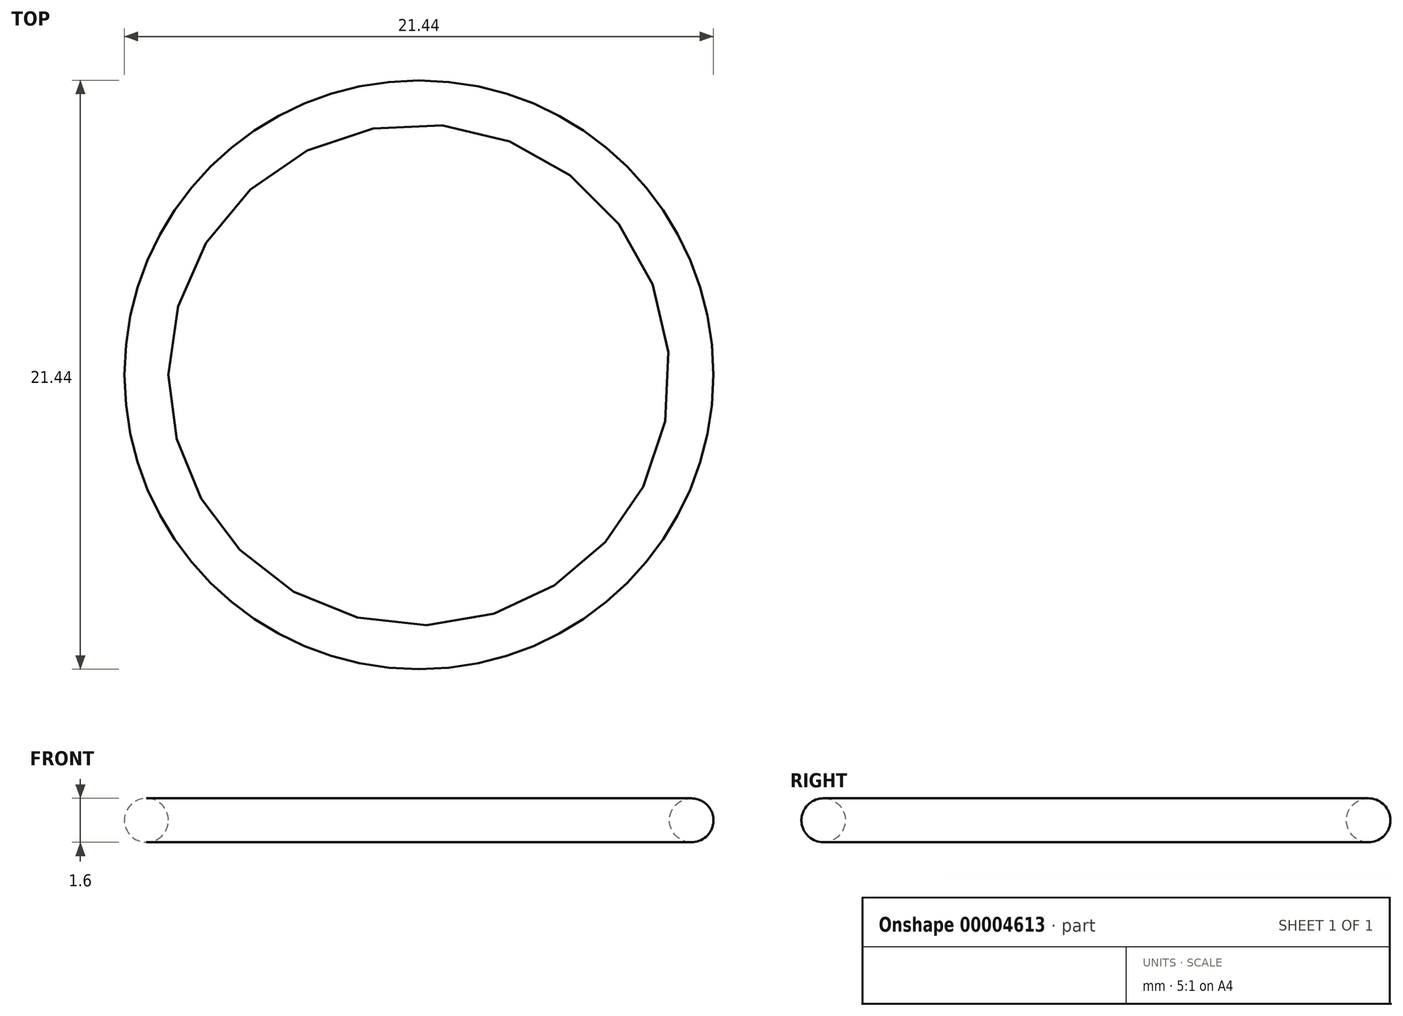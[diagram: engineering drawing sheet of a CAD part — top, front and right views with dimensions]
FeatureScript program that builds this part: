
annotation { "Feature Type Name" : "Feature", "Feature Type Description" : "" }
export const myFeature = defineFeature(function(context is Context, id is Id, definition is map)
    precondition{}
    {
        {
            var Q0;
            Q0=qCreatedBy(makeId("Front.planeOp"),FACE);
            var sketch = newSketch(context, id + "F0", { "sketchPlane" : qUnion([Q0])});
            skCircle(sketch, "E0", {"center": v(9.92, 0) * mm, "radius": 0.8 * mm});
            skLineSegment(sketch, "E1", {"start": v(0, 0) * mm, "end": v(0, 6.26) * mm, "construction": true});
            skPoint(sketch, "E2", {"position": v(10.72, 0) * mm});
            skSolve(sketch);
        }
        {
            var Q0;
            Q0=makeQuery(id+"F0.imprint","IMPRINT",FACE,{"disambiguationData":[TD([[makeQuery(id+"F0.imprint","IMPRINT",EDGE,{"derivedFrom":sQuery(id+"F0.wireOp",EDGE,"E0")}),1.0]])]});
            var Q1;
            Q1=sQuery(id+"F0.wireOp",EDGE,"E1");
            revolve(context, id + "F1", {"entities" : qUnion([Q0]), "axis" : qUnion([Q1]), "revolveType" : RevolveType.FULL});
        }
    });
